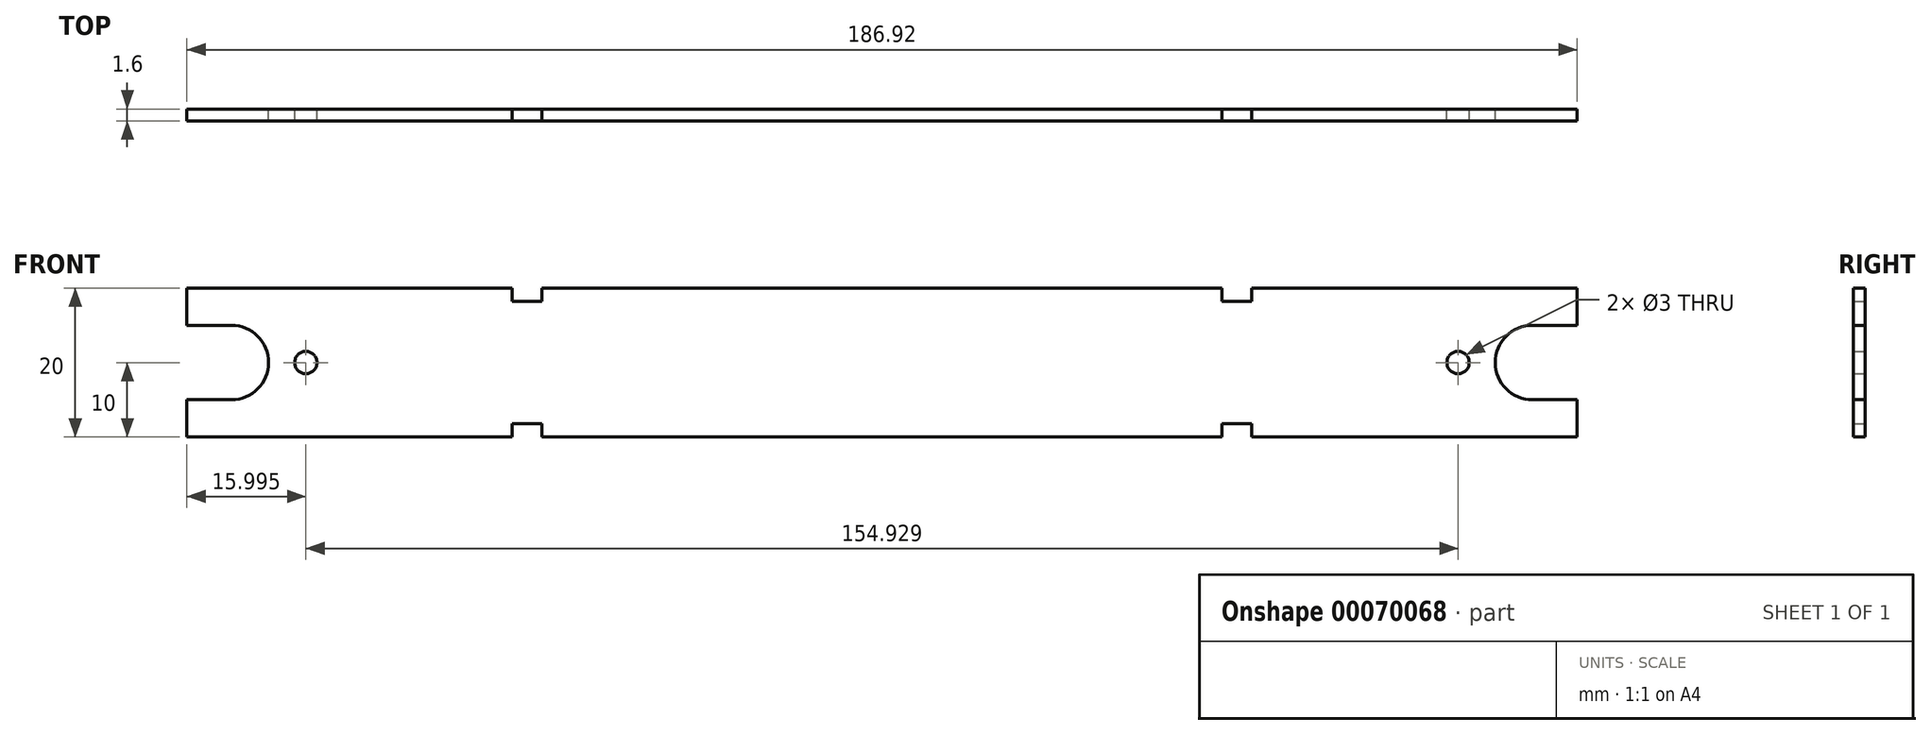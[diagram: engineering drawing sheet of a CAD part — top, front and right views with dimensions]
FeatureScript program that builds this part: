
annotation { "Feature Type Name" : "Feature", "Feature Type Description" : "" }
export const myFeature = defineFeature(function(context is Context, id is Id, definition is map)
    precondition{}
    {
        {
            var Q0;
            Q0=qCreatedBy(makeId("Front.planeOp"),FACE);
            var sketch = newSketch(context, id + "F0", { "sketchPlane" : qUnion([Q0])});
            skLineSegment(sketch, "E0", {"start": v(-87.46, 0) * mm, "end": v(87.46, 0) * mm, "construction": true});
            skCircle(sketch, "E1", {"center": v(-87.46, 0) * mm, "radius": 4 * mm, "construction": true});
            skCircle(sketch, "E2", {"center": v(87.46, 0) * mm, "radius": 4 * mm, "construction": true});
            skLineSegment(sketch, "E3.bottom", {"start": v(-93.46, 6) * mm, "end": v(-81.46, 6) * mm, "construction": true});
            skLineSegment(sketch, "E3.top", {"start": v(-93.46, -6) * mm, "end": v(-81.46, -6) * mm, "construction": true});
            skLineSegment(sketch, "E3.left", {"start": v(-93.46, 6) * mm, "end": v(-93.46, -6) * mm, "construction": true});
            skLineSegment(sketch, "E3.right", {"start": v(-81.46, 6) * mm, "end": v(-81.46, -6) * mm, "construction": true});
            skLineSegment(sketch, "E4.bottom", {"start": v(93.46, 6) * mm, "end": v(81.46, 6) * mm, "construction": true});
            skLineSegment(sketch, "E4.top", {"start": v(93.46, -6) * mm, "end": v(81.46, -6) * mm, "construction": true});
            skLineSegment(sketch, "E4.left", {"start": v(93.46, 6) * mm, "end": v(93.46, -6) * mm, "construction": true});
            skLineSegment(sketch, "E4.right", {"start": v(81.46, 6) * mm, "end": v(81.46, -6) * mm, "construction": true});
            skLineSegment(sketch, "E5", {"start": v(0, 10) * mm, "end": v(0, -10) * mm, "construction": true});
            skLineSegment(sketch, "E6", {"start": v(-18, 0) * mm, "end": v(18, 0) * mm, "construction": true});
            skLineSegment(sketch, "E7.bottom", {"start": v(-36.23, -6.25) * mm, "end": v(-59.23, -6.25) * mm, "construction": true});
            skLineSegment(sketch, "E7.top", {"start": v(-36.23, 6.25) * mm, "end": v(-59.23, 6.25) * mm, "construction": true});
            skLineSegment(sketch, "E7.left", {"start": v(-36.23, -6.25) * mm, "end": v(-36.23, 6.25) * mm, "construction": true});
            skLineSegment(sketch, "E7.right", {"start": v(-59.23, -6.25) * mm, "end": v(-59.23, 6.25) * mm, "construction": true});
            skPoint(sketch, "E7.middle", {"position": v(-47.73, 0) * mm});
            skPoint(sketch, "E8", {"position": v(-81.46, 0) * mm});
            skPoint(sketch, "E9", {"position": v(81.46, 0) * mm});
            skLineSegment(sketch, "E10.bottom", {"start": v(59.23, 6.25) * mm, "end": v(36.23, 6.25) * mm, "construction": true});
            skLineSegment(sketch, "E10.top", {"start": v(59.23, -6.25) * mm, "end": v(36.23, -6.25) * mm, "construction": true});
            skLineSegment(sketch, "E10.left", {"start": v(59.23, 6.25) * mm, "end": v(59.23, -6.25) * mm, "construction": true});
            skLineSegment(sketch, "E10.right", {"start": v(36.23, 6.25) * mm, "end": v(36.23, -6.25) * mm, "construction": true});
            skPoint(sketch, "E10.middle", {"position": v(47.73, 0) * mm});
            skCircle(sketch, "E11", {"center": v(-77.46, 0) * mm, "radius": 1.5 * mm});
            skCircle(sketch, "E12", {"center": v(-87.46, 0) * mm, "radius": 5 * mm, "construction": true});
            skLineSegment(sketch, "E13", {"start": v(-47.73, 0) * mm, "end": v(-47.73, 8.25) * mm, "construction": true});
            skCircle(sketch, "E14.MirrorC", {"center": v(77.46, 0) * mm, "radius": 1.5 * mm});
            skCircle(sketch, "E15.MirrorC", {"center": v(87.46, 0) * mm, "radius": 5 * mm, "construction": true});
            skLineSegment(sketch, "E16", {"start": v(-49.73, 8.25) * mm, "end": v(-45.73, 8.25) * mm});
            skLineSegment(sketch, "E17", {"start": v(0, 10) * mm, "end": v(-45.73, 10) * mm});
            skLineSegment(sketch, "E18", {"start": v(-45.73, 10) * mm, "end": v(-45.73, 8.25) * mm});
            skLineSegment(sketch, "E19", {"start": v(-49.73, 8.25) * mm, "end": v(-49.73, 10) * mm});
            skLineSegment(sketch, "E20", {"start": v(-49.73, 10) * mm, "end": v(-93.46, 10) * mm});
            skArc(sketch, "E21", {"start": v(-82.46, 0) * mm, "mid": v(-83.93, 3.54) * mm, "end": v(-87.46, 5) * mm});
            skLineSegment(sketch, "E22", {"start": v(-87.46, 5) * mm, "end": v(-93.46, 5) * mm});
            skLineSegment(sketch, "E23", {"start": v(-93.46, 5) * mm, "end": v(-93.46, 10) * mm});
            skLineSegment(sketch, "E24.MirrorCS", {"start": v(0, -10) * mm, "end": v(-45.73, -10) * mm});
            skLineSegment(sketch, "E25.MirrorCS", {"start": v(-49.73, -8.25) * mm, "end": v(-45.73, -8.25) * mm});
            skLineSegment(sketch, "E26.MirrorCS", {"start": v(-45.73, -10) * mm, "end": v(-45.73, -8.25) * mm});
            skLineSegment(sketch, "E27.MirrorCS", {"start": v(-49.73, -8.25) * mm, "end": v(-49.73, -10) * mm});
            skLineSegment(sketch, "E28.MirrorCS", {"start": v(-49.73, -10) * mm, "end": v(-93.46, -10) * mm});
            skLineSegment(sketch, "E29.MirrorCS", {"start": v(-93.46, -5) * mm, "end": v(-93.46, -10) * mm});
            skLineSegment(sketch, "E30.MirrorCS", {"start": v(-87.46, -5) * mm, "end": v(-93.46, -5) * mm});
            skArc(sketch, "E31.MirrorCS", {"start": v(-82.46, 0) * mm, "mid": v(-83.93, -3.54) * mm, "end": v(-87.46, -5) * mm});
            skLineSegment(sketch, "E32.MirrorCS", {"start": v(49.73, 10) * mm, "end": v(93.46, 10) * mm});
            skLineSegment(sketch, "E33.MirrorCS", {"start": v(93.46, 5) * mm, "end": v(93.46, 10) * mm});
            skLineSegment(sketch, "E34.MirrorCS", {"start": v(87.46, 5) * mm, "end": v(93.46, 5) * mm});
            skArc(sketch, "E35.MirrorCS", {"start": v(82.46, 0) * mm, "mid": v(83.93, 3.54) * mm, "end": v(87.46, 5) * mm});
            skArc(sketch, "E36.MirrorCS", {"start": v(82.46, 0) * mm, "mid": v(83.93, -3.54) * mm, "end": v(87.46, -5) * mm});
            skLineSegment(sketch, "E37.MirrorCS", {"start": v(87.46, -5) * mm, "end": v(93.46, -5) * mm});
            skLineSegment(sketch, "E38.MirrorCS", {"start": v(93.46, -5) * mm, "end": v(93.46, -10) * mm});
            skLineSegment(sketch, "E39.MirrorCS", {"start": v(49.73, -10) * mm, "end": v(93.46, -10) * mm});
            skLineSegment(sketch, "E40.MirrorCS", {"start": v(49.73, -8.25) * mm, "end": v(45.73, -8.25) * mm});
            skLineSegment(sketch, "E41.MirrorCS", {"start": v(49.73, -8.25) * mm, "end": v(49.73, -10) * mm});
            skLineSegment(sketch, "E42.MirrorCS", {"start": v(45.73, -10) * mm, "end": v(45.73, -8.25) * mm});
            skLineSegment(sketch, "E43.MirrorCS", {"start": v(0, -10) * mm, "end": v(45.73, -10) * mm});
            skLineSegment(sketch, "E44.MirrorCS", {"start": v(0, 10) * mm, "end": v(45.73, 10) * mm});
            skLineSegment(sketch, "E45.MirrorCS", {"start": v(49.73, 8.25) * mm, "end": v(45.73, 8.25) * mm});
            skLineSegment(sketch, "E46.MirrorCS", {"start": v(49.73, 8.25) * mm, "end": v(49.73, 10) * mm});
            skLineSegment(sketch, "E47.MirrorCS", {"start": v(45.73, 10) * mm, "end": v(45.73, 8.25) * mm});
            skSolve(sketch);
        }
        {
            var Q0;
            Q0 = qSketchRegion(id + "F0", true);
            extrude(context, id + "F1", {"entities" : qUnion([Q0]), "depth" : 1.6 * mm});
        }
    });
